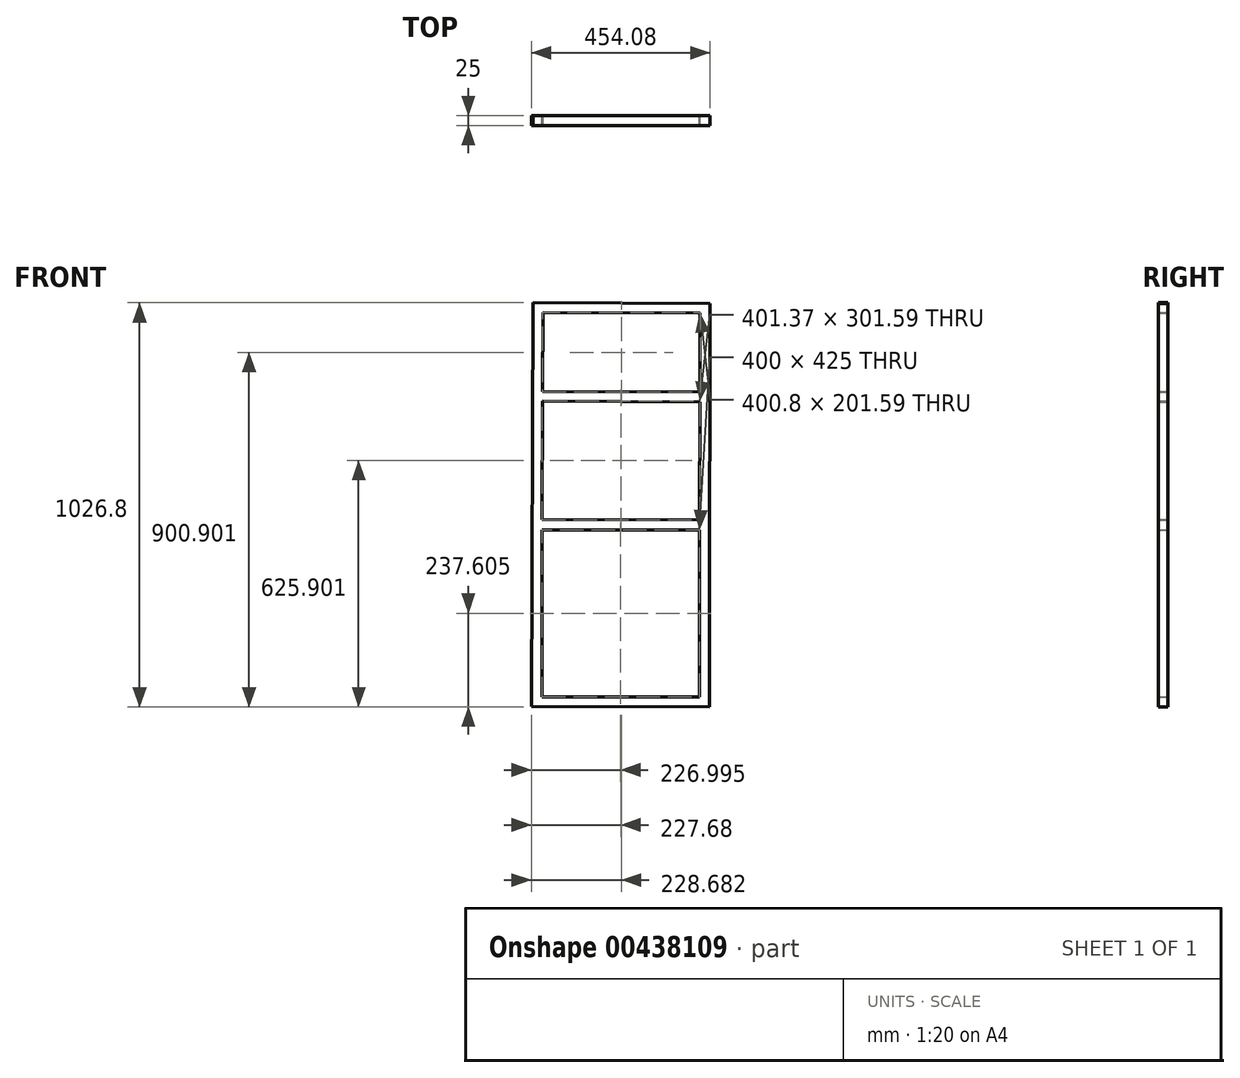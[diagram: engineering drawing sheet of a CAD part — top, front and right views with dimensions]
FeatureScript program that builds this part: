
annotation { "Feature Type Name" : "Feature", "Feature Type Description" : "" }
export const myFeature = defineFeature(function(context is Context, id is Id, definition is map)
    precondition{}
    {
        {
            var Q0;
            Q0=qCreatedBy(makeId("Front.planeOp"),FACE);
            var sketch = newSketch(context, id + "F0", { "sketchPlane" : qUnion([Q0])});
            skLineSegment(sketch, "E0", {"start": v(-170.27, 175.07) * mm, "end": v(229.73, 173.47) * mm});
            skLineSegment(sketch, "E1", {"start": v(-171.56, -149.93) * mm, "end": v(228.44, -151.53) * mm});
            skLineSegment(sketch, "E2.0", {"start": v(-169.47, 375.07) * mm, "end": v(230.53, 373.47) * mm});
            skLineSegment(sketch, "E3", {"start": v(230.53, 373.47) * mm, "end": v(229.73, 173.47) * mm});
            skLineSegment(sketch, "E4", {"start": v(229.82, 148.47) * mm, "end": v(228.44, -151.53) * mm});
            skLineSegment(sketch, "E5", {"start": v(229.82, 148.47) * mm, "end": v(-170.36, 150.07) * mm});
            skLineSegment(sketch, "E6.0", {"start": v(255.53, 373.37) * mm, "end": v(254.73, 173.14) * mm});
            skLineSegment(sketch, "E7.0", {"start": v(254.81, 148.36) * mm, "end": v(253.44, -152.56) * mm});
            skLineSegment(sketch, "E8", {"start": v(255.53, 373.37) * mm, "end": v(255.53, 398.37) * mm});
            skLineSegment(sketch, "E9", {"start": v(-169.47, 375.07) * mm, "end": v(-170.27, 175.07) * mm});
            skLineSegment(sketch, "E10", {"start": v(-170.36, 150.07) * mm, "end": v(-171.56, -149.93) * mm});
            skLineSegment(sketch, "E11", {"start": v(254.81, 148.36) * mm, "end": v(254.73, 173.14) * mm});
            skLineSegment(sketch, "E12.bottom", {"start": v(-171.56, -176.53) * mm, "end": v(228.44, -176.53) * mm});
            skLineSegment(sketch, "E12.top", {"start": v(-171.56, -601.53) * mm, "end": v(228.44, -601.53) * mm});
            skLineSegment(sketch, "E12.left", {"start": v(-171.56, -176.53) * mm, "end": v(-171.56, -601.53) * mm});
            skLineSegment(sketch, "E12.right", {"start": v(228.44, -176.53) * mm, "end": v(228.44, -601.53) * mm});
            skLineSegment(sketch, "E13", {"start": v(253.44, -152.56) * mm, "end": v(253.44, -626.63) * mm});
            skLineSegment(sketch, "E14", {"start": v(-198.55, -624.83) * mm, "end": v(253.44, -626.63) * mm});
            skLineSegment(sketch, "E15", {"start": v(-194.47, 400.17) * mm, "end": v(255.53, 398.37) * mm});
            skLineSegment(sketch, "E16", {"start": v(-194.47, 400.17) * mm, "end": v(-198.55, -624.83) * mm});
            skSolve(sketch);
        }
        {
            var Q0;
            Q0=qSketchRegion(id+"F0",true);
            extrude(context, id + "F1", {"entities" : qUnion([Q0]), "endBound" : BoundingType.SYMMETRIC, "depth" : 25 * mm});
        }
    });
